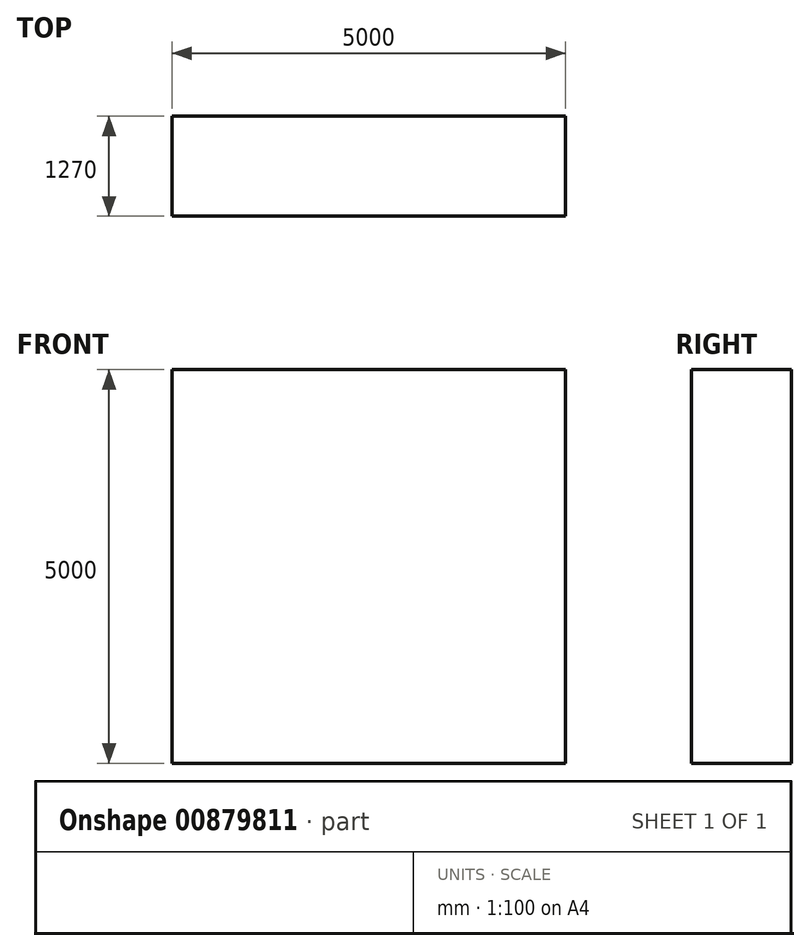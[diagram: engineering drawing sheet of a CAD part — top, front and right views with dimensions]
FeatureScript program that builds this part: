
annotation { "Feature Type Name" : "Feature", "Feature Type Description" : "" }
export const myFeature = defineFeature(function(context is Context, id is Id, definition is map)
    precondition{}
    {
        {
            var Q0;
            Q0=qCreatedBy(makeId("Front.planeOp"),FACE);
            var sketch = newSketch(context, id + "F0", { "sketchPlane" : qUnion([Q0])});
            skLineSegment(sketch, "E0.bottom", {"start": v(2500, -2500) * mm, "end": v(-2500, -2500) * mm});
            skLineSegment(sketch, "E0.top", {"start": v(2500, 2500) * mm, "end": v(-2500, 2500) * mm});
            skLineSegment(sketch, "E0.left", {"start": v(2500, -2500) * mm, "end": v(2500, 2500) * mm});
            skLineSegment(sketch, "E0.right", {"start": v(-2500, -2500) * mm, "end": v(-2500, 2500) * mm});
            skPoint(sketch, "E0.middle", {"position": v(0, 0) * mm});
            skSolve(sketch);
        }
        {
            var Q0;
            Q0=makeQuery(id+"F0.imprint","IMPRINT",FACE,{"disambiguationData":[TD([[makeQuery(id+"F0.imprint","IMPRINT",EDGE,{"derivedFrom":sQuery(id+"F0.wireOp",EDGE,"E0.bottom")}),-1.0]])]});
            extrude(context, id + "F1", {"entities" : qUnion([Q0]), "endBound" : BoundingType.SYMMETRIC, "depth" : 1270 * mm, "offsetDistance" : 25.4 * mm});
        }
    });
